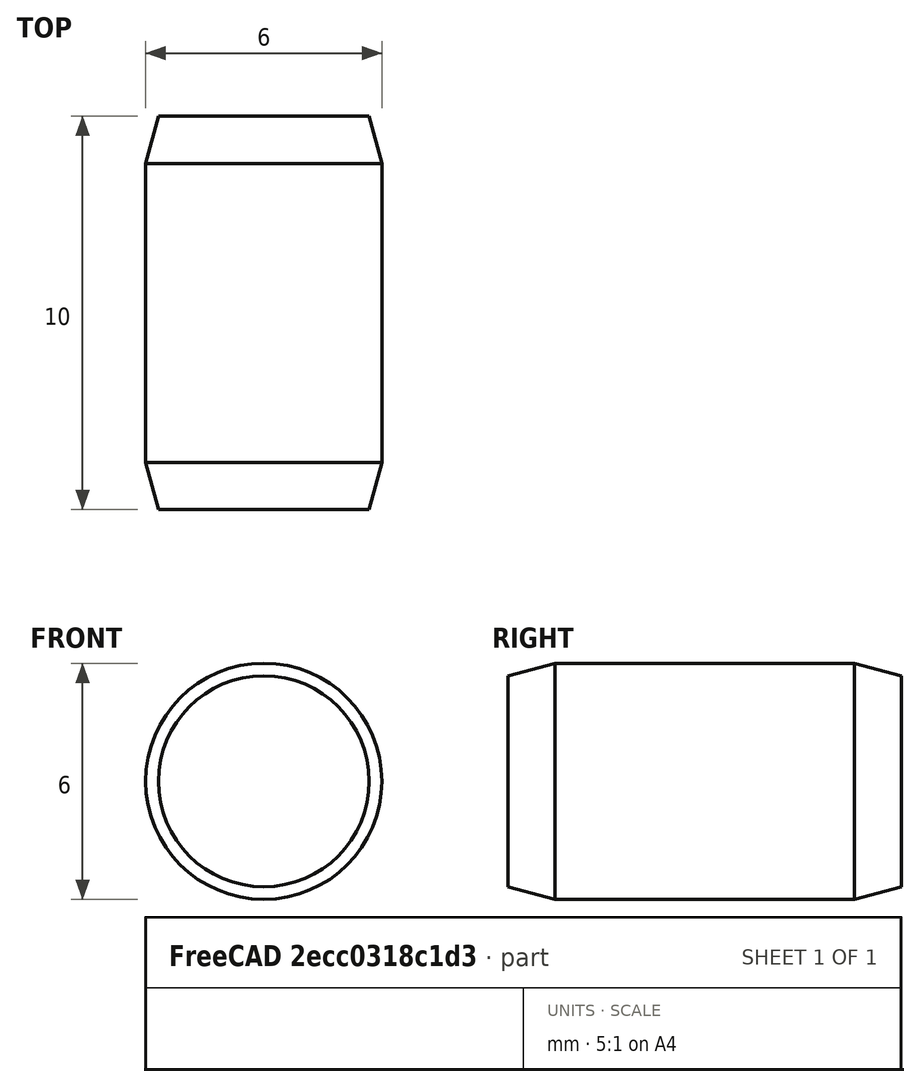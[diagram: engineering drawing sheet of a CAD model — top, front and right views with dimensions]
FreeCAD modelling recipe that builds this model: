
FCSTD DOCUMENT  (FreeCAD 0.15R4470 (Git))
Label: Zyl-Stift_ISO_2338-6x10
License: CC-BY 3.0
LicenseURL: http://creativecommons.org/licenses/by/3.0/
objects: Sketcher::SketchObject×1, PartDesign::Revolution×1
note: 3 computed .brp shape members not serialized (recipe doc carries the construction recipe); baked Part::Feature solids carry a one-line shape summary decoded from their .brp

FEATURE [Sketcher::SketchObject] Sketch
  Placement = pos=(0,0,0) rot=(0.57735,0.57735,0.57735;2.0944rad)
  sketch-geometry (7):
    g0: LineSegment StartX=0 StartY=0 StartZ=0 EndX=0 EndY=2.67846 EndZ=0
    g1: LineSegment StartX=0 StartY=2.67846 StartZ=0 EndX=1.2 EndY=3 EndZ=0
    g2: LineSegment StartX=1.2 StartY=3 StartZ=0 EndX=8.8 EndY=3 EndZ=0
    g3: LineSegment StartX=8.8 StartY=3 StartZ=0 EndX=10 EndY=2.67846 EndZ=0
    g4: LineSegment StartX=10 StartY=2.67846 StartZ=0 EndX=10 EndY=0 EndZ=0
    g5: LineSegment StartX=10 StartY=0 StartZ=0 EndX=0 EndY=0 EndZ=0
    g6: LineSegment [constr] StartX=0 StartY=2.67846 StartZ=0 EndX=10 EndY=2.67846 EndZ=0
  constraints (19):
    c: Coincident(g0,g-1)
    c: PointOnObject(g0,g-2)
    c: Coincident(g0,g1)
    c: Coincident(g1,g2)
    c: Horizontal(g2)
    c: Coincident(g2,g3)
    c: Coincident(g3,g4)
    c: Vertical(g4)
    c: Coincident(g4,g5)
    c: Coincident(g5,g-1)
    c: Horizontal(g5)
    c: Equal(g3,g1)
    c: Coincident(g6,g0)
    c: Coincident(g6,g3)
    c: Horizontal(g6)
    c: Angle(g6,g1) = 0.261799
    c: DistanceY(g-1,g1) = 3
    c: DistanceX(g5) = -10
    c: DistanceX(g1) = 1.2
FEATURE [PartDesign::Revolution] Revolution  label="Zyl-Stift ISO 2338-6x10 #"
  Angle = 360
  Axis = (0,1,0)
  Base = (0,0,0)
  Placement = pos=(0,0,0) rot=(0.57735,0.57735,0.57735;2.0944rad)
  ReferenceAxis = -> Sketch [H_Axis]
  Sketch = -> Sketch
